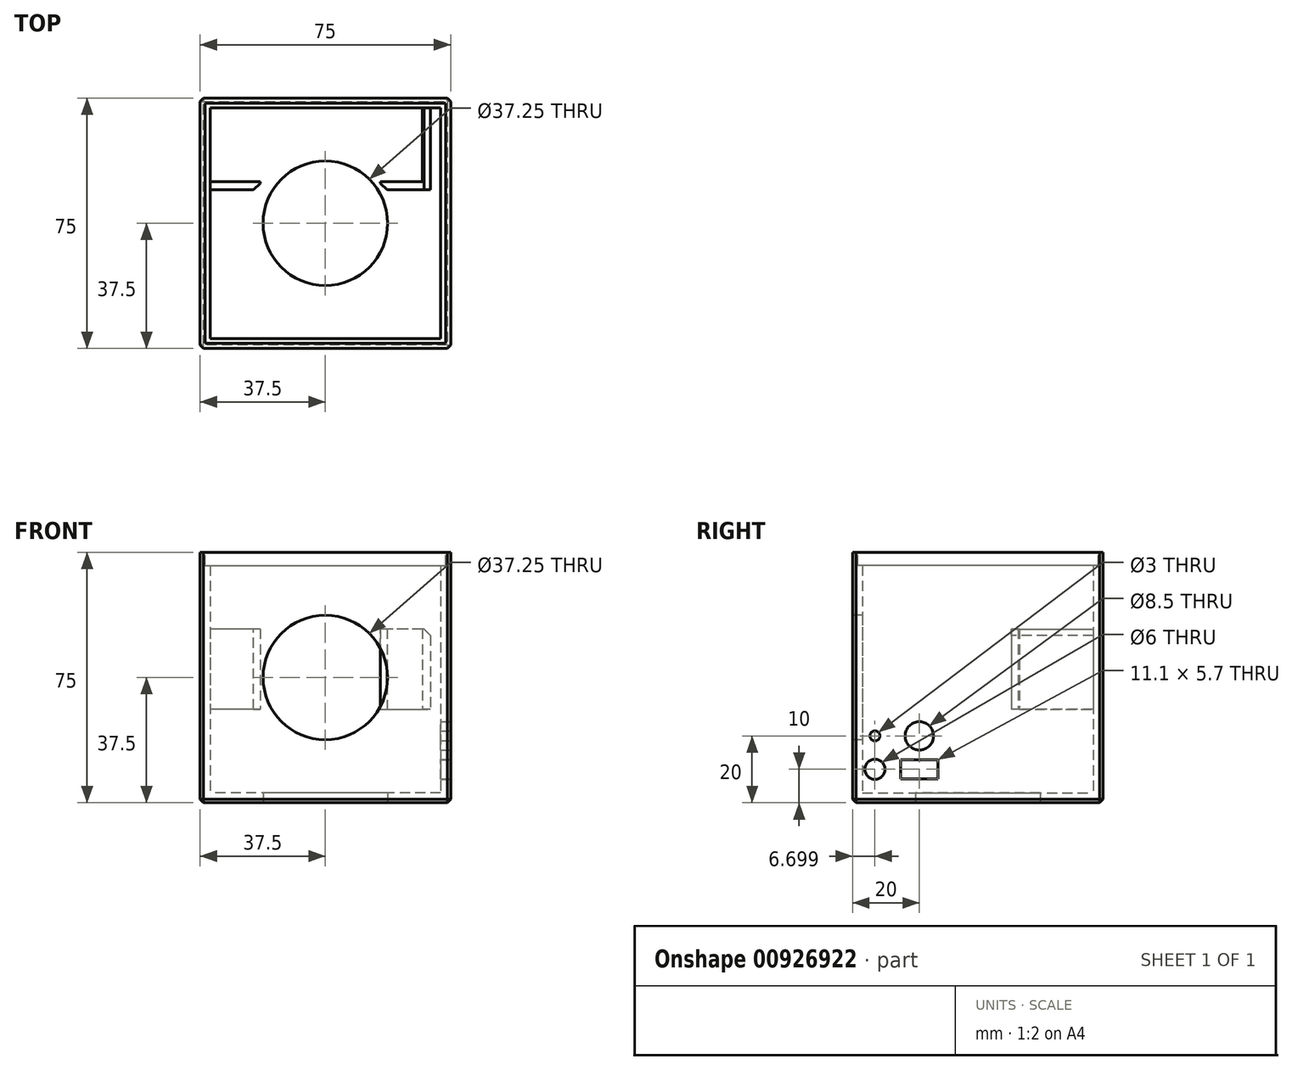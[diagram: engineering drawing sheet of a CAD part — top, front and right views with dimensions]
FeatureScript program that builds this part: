
annotation { "Feature Type Name" : "Feature", "Feature Type Description" : "" }
export const myFeature = defineFeature(function(context is Context, id is Id, definition is map)
    precondition{}
    {
        {
            var Q0;
            Q0=qCreatedBy(makeId("Top.planeOp"),FACE);
            var sketch = newSketch(context, id + "F0", { "sketchPlane" : qUnion([Q0])});
            skLineSegment(sketch, "E0.bottom", {"start": v(-37.5, 37.5) * mm, "end": v(37.5, 37.5) * mm});
            skLineSegment(sketch, "E0.top", {"start": v(-37.5, -37.5) * mm, "end": v(37.5, -37.5) * mm});
            skLineSegment(sketch, "E0.left", {"start": v(-37.5, 37.5) * mm, "end": v(-37.5, -37.5) * mm});
            skLineSegment(sketch, "E0.right", {"start": v(37.5, 37.5) * mm, "end": v(37.5, -37.5) * mm});
            skPoint(sketch, "E0.middle", {"position": v(0, 0) * mm});
            skLineSegment(sketch, "E1.0", {"start": v(-34.5, 34.5) * mm, "end": v(34.5, 34.5) * mm});
            skLineSegment(sketch, "E1.1", {"start": v(-34.5, 34.5) * mm, "end": v(-34.5, -34.5) * mm});
            skLineSegment(sketch, "E1.2", {"start": v(-34.5, -34.5) * mm, "end": v(34.5, -34.5) * mm});
            skLineSegment(sketch, "E1.3", {"start": v(34.5, 34.5) * mm, "end": v(34.5, -34.5) * mm});
            skLineSegment(sketch, "E2.right", {"start": v(29, 34.5) * mm, "end": v(29, 12.5) * mm});
            skLineSegment(sketch, "E3.0", {"start": v(31.5, 34.5) * mm, "end": v(31.5, 10) * mm});
            skLineSegment(sketch, "E4", {"start": v(-19.5, 12.5) * mm, "end": v(-19.5, 10) * mm});
            skLineSegment(sketch, "E5", {"start": v(16.5, 12.5) * mm, "end": v(16.5, 10) * mm});
            skLineSegment(sketch, "E6", {"start": v(-19.5, 10) * mm, "end": v(-34.5, 10) * mm});
            skLineSegment(sketch, "E7", {"start": v(-19.5, 12.5) * mm, "end": v(-34.5, 12.5) * mm});
            skLineSegment(sketch, "E8", {"start": v(16.5, 10) * mm, "end": v(31.5, 10) * mm});
            skLineSegment(sketch, "E9", {"start": v(16.5, 12.5) * mm, "end": v(29, 12.5) * mm});
            skCircle(sketch, "E10", {"center": v(0, 0) * mm, "radius": 18.62 * mm});
            skSolve(sketch);
        }
        {
            var Q0;
            Q0=makeQuery(id+"F0.imprint","IMPRINT",FACE,{"disambiguationData":[TD([[makeQuery(id+"F0.imprint","IMPRINT",EDGE,{"derivedFrom":sQuery(id+"F0.wireOp",EDGE,"E1.0")}),-1.0]])]});
            var Q1;
            Q1=makeQuery(id+"F0.imprint","IMPRINT",FACE,{"disambiguationData":[TD([[makeQuery(id+"F0.imprint","IMPRINT",EDGE,{"derivedFrom":sQuery(id+"F0.wireOp",EDGE,"E0.bottom")}),-1.0]])]});
            var Q2;
            {var subQ0=sQuery(id+"F0.wireOp",EDGE,"E1.2");Q2=makeQuery(id+"F0.imprint","IMPRINT",FACE,{"disambiguationData":[TD([[makeQuery(id+"F0.imprint","IMPRINT",EDGE,{"derivedFrom":subQ0}),1.0]])]});}
            var Q3;
            {var subQ0=sQuery(id+"F0.wireOp",EDGE,"E2.top");Q3=makeQuery(id+"F0.imprint","IMPRINT",FACE,{"disambiguationData":[TD([[makeQuery(id+"F0.imprint","IMPRINT",EDGE,{"derivedFrom":subQ0}),-1.0]])]});}
            extrude(context, id + "F1", {"entities" : qUnion([Q0, Q1, Q2, Q3]), "depth" : 3 * mm, "offsetDistance" : 25 * mm});
        }
        {
            var Q0;
            Q0=makeQuery(id+"F0.imprint","IMPRINT",FACE,{"disambiguationData":[TD([[makeQuery(id+"F0.imprint","IMPRINT",EDGE,{"derivedFrom":sQuery(id+"F0.wireOp",EDGE,"E0.bottom")}),-1.0]])]});
            extrude(context, id + "F2", {"entities" : qUnion([Q0]), "operationType" : NewBodyOperationType.ADD, "depth" : 75 * mm, "offsetDistance" : 25 * mm});
        }
        {
            var Q0;
            {var subQ0=sQuery(id+"F0.wireOp",EDGE,"E0.top");Q0=makeQuery(id+"F2.boolean.opBoolean","MERGE",FACE,{"derivedFrom":[makeQuery(id+"F1.opExtrude","SWEPT_FACE",FACE,{"disambiguationData":[OSD([subQ0])]}),makeQuery(id+"F2.opExtrude","SWEPT_FACE",FACE,{"disambiguationData":[OSD([subQ0])]})]});}
            var sketch = newSketch(context, id + "F3", { "sketchPlane" : qUnion([Q0])});
            skCircle(sketch, "E11", {"center": v(0, 37.5) * mm, "radius": 18.62 * mm});
            skSolve(sketch);
        }
        {
            var Q0;
            Q0=makeQuery(id+"F3.imprint","IMPRINT",FACE,{"disambiguationData":[TD([[makeQuery(id+"F3.imprint","IMPRINT",EDGE,{"derivedFrom":sQuery(id+"F3.wireOp",EDGE,"E11")}),1.0]])]});
            extrude(context, id + "F4", {"entities" : qUnion([Q0]), "operationType" : NewBodyOperationType.REMOVE, "oppositeDirection" : true, "depth" : 10.2 * mm, "offsetDistance" : 25 * mm});
        }
        {
            var Q0;
            {var subQ0=sQuery(id+"F0.wireOp",EDGE,"E2.top");Q0=makeQuery(id+"F0.imprint","IMPRINT",FACE,{"disambiguationData":[TD([[makeQuery(id+"F0.imprint","IMPRINT",EDGE,{"derivedFrom":subQ0}),-1.0]])]});}
            var Q1;
            Q1=makeQuery(id+"F0.imprint","IMPRINT",FACE,{"disambiguationData":[TD([[makeQuery(id+"F0.imprint","IMPRINT",EDGE,{"derivedFrom":sQuery(id+"F0.wireOp",EDGE,"E4")}),-1.0]])]});
            var Q2;
            {var subQ1=sQuery(id+"F0.wireOp",EDGE,"E2.right");Q2=makeQuery(id+"F0.imprint","IMPRINT",FACE,{"disambiguationData":[TD([[makeQuery(id+"F0.imprint","IMPRINT",EDGE,{"derivedFrom":subQ1}),1.0]])]});}
            extrude(context, id + "F5", {"entities" : qUnion([Q0, Q1, Q2]), "operationType" : NewBodyOperationType.ADD, "depth" : 77 * mm, "offsetDistance" : 25 * mm});
        }
        {
            var Q0;
            Q0=makeQuery(id+"F2.opExtrude","CAP_FACE",FACE,{"disambiguationData":[OSD([sQuery(id+"F0.wireOp",EDGE,"E0.bottom"),sQuery(id+"F0.wireOp",EDGE,"E0.top"),sQuery(id+"F0.wireOp",EDGE,"E0.left"),sQuery(id+"F0.wireOp",EDGE,"E0.right"),sQuery(id+"F0.wireOp",EDGE,"E1.0"),sQuery(id+"F0.wireOp",EDGE,"E1.1"),sQuery(id+"F0.wireOp",EDGE,"E1.2"),sQuery(id+"F0.wireOp",EDGE,"E1.3")])],"isStart":false});
            var sketch = newSketch(context, id + "F6", { "sketchPlane" : qUnion([Q0])});
            skLineSegment(sketch, "E12.bottom", {"start": v(-36, 36) * mm, "end": v(36, 36) * mm});
            skLineSegment(sketch, "E12.top", {"start": v(-36, -36) * mm, "end": v(36, -36) * mm});
            skLineSegment(sketch, "E12.left", {"start": v(-36, 36) * mm, "end": v(-36, -36) * mm});
            skLineSegment(sketch, "E12.right", {"start": v(36, 36) * mm, "end": v(36, -36) * mm});
            skPoint(sketch, "E12.middle", {"position": v(0, 0) * mm});
            skSolve(sketch);
        }
        {
            var Q0;
            Q0=makeQuery(id+"F6.imprint","IMPRINT",FACE,{"disambiguationData":[TD([[makeQuery(id+"F6.imprint","IMPRINT",EDGE,{"derivedFrom":sQuery(id+"F6.wireOp",EDGE,"E12.bottom")}),-1.0]])]});
            extrude(context, id + "F7", {"entities" : qUnion([Q0]), "operationType" : NewBodyOperationType.REMOVE, "oppositeDirection" : true, "depth" : 4 * mm, "offsetDistance" : 25 * mm});
        }
        {
            var Q0;
            Q0=makeQuery(id+"F1.opExtrude","CAP_EDGE",EDGE,{"disambiguationData":[OSD([sQuery(id+"F0.wireOp",EDGE,"E0.right")])],"isStart":true});
            var Q1;
            Q1=makeQuery(id+"F1.opExtrude","CAP_EDGE",EDGE,{"disambiguationData":[OSD([sQuery(id+"F0.wireOp",EDGE,"E0.top")])],"isStart":true});
            var Q2;
            {var subQ0=sQuery(id+"F0.wireOp",EDGE,"E0.left");var subQ1=sQuery(id+"F0.wireOp",EDGE,"E0.top");Q2=makeQuery(id+"F2.boolean.opBoolean","MERGE",EDGE,{"derivedFrom":[makeQuery(id+"F1.opExtrude","SWEPT_EDGE",EDGE,{"disambiguationData":[OSD([subQ1,subQ0])]}),makeQuery(id+"F2.opExtrude","SWEPT_EDGE",EDGE,{"disambiguationData":[OSD([subQ1,subQ0])]})]});}
            var Q3;
            {var subQ0=sQuery(id+"F0.wireOp",EDGE,"E0.right");var subQ1=sQuery(id+"F0.wireOp",EDGE,"E0.top");Q3=makeQuery(id+"F2.boolean.opBoolean","MERGE",EDGE,{"derivedFrom":[makeQuery(id+"F1.opExtrude","SWEPT_EDGE",EDGE,{"disambiguationData":[OSD([subQ1,subQ0])]}),makeQuery(id+"F2.opExtrude","SWEPT_EDGE",EDGE,{"disambiguationData":[OSD([subQ1,subQ0])]})]});}
            var Q4;
            Q4=makeQuery(id+"F1.opExtrude","CAP_EDGE",EDGE,{"disambiguationData":[OSD([sQuery(id+"F0.wireOp",EDGE,"E0.left")])],"isStart":true});
            var Q5;
            Q5=makeQuery(id+"F1.opExtrude","CAP_EDGE",EDGE,{"disambiguationData":[OSD([sQuery(id+"F0.wireOp",EDGE,"E0.bottom")])],"isStart":true});
            var Q6;
            {var subQ0=sQuery(id+"F0.wireOp",EDGE,"E0.right");var subQ1=sQuery(id+"F0.wireOp",EDGE,"E0.bottom");Q6=makeQuery(id+"F2.boolean.opBoolean","MERGE",EDGE,{"derivedFrom":[makeQuery(id+"F1.opExtrude","SWEPT_EDGE",EDGE,{"disambiguationData":[OSD([subQ1,subQ0])]}),makeQuery(id+"F2.opExtrude","SWEPT_EDGE",EDGE,{"disambiguationData":[OSD([subQ1,subQ0])]})]});}
            var Q7;
            {var subQ0=sQuery(id+"F0.wireOp",EDGE,"E0.left");var subQ1=sQuery(id+"F0.wireOp",EDGE,"E0.bottom");Q7=makeQuery(id+"F2.boolean.opBoolean","MERGE",EDGE,{"derivedFrom":[makeQuery(id+"F1.opExtrude","SWEPT_EDGE",EDGE,{"disambiguationData":[OSD([subQ1,subQ0])]}),makeQuery(id+"F2.opExtrude","SWEPT_EDGE",EDGE,{"disambiguationData":[OSD([subQ1,subQ0])]})]});}
            chamfer(context, id + "F8", {"entities" : qUnion([Q0, Q1, Q2, Q3, Q4, Q5, Q6, Q7]), "width" : 1 * mm});
        }
        {
            var Q0;
            Q0=makeQuery(id+"F5.opExtrude","SWEPT_FACE",FACE,{"disambiguationData":[OSD([sQuery(id+"F0.wireOp",EDGE,"E6")])]});
            var sketch = newSketch(context, id + "F9", { "sketchPlane" : qUnion([Q0])});
            skLineSegment(sketch, "E13", {"start": v(-34.5, 77) * mm, "end": v(-19.5, 77) * mm});
            skLineSegment(sketch, "E14", {"start": v(-19.5, 77) * mm, "end": v(-19.5, 52) * mm});
            skLineSegment(sketch, "E15", {"start": v(-19.5, 52) * mm, "end": v(-34.5, 52) * mm});
            skLineSegment(sketch, "E16", {"start": v(-34.5, 52) * mm, "end": v(-34.5, 77) * mm});
            skLineSegment(sketch, "E17", {"start": v(-19.5, 3) * mm, "end": v(-19.5, 28) * mm});
            skLineSegment(sketch, "E18", {"start": v(-19.5, 28) * mm, "end": v(-34.5, 28) * mm});
            skLineSegment(sketch, "E19", {"start": v(-34.5, 28) * mm, "end": v(-34.5, 3) * mm});
            skLineSegment(sketch, "E20", {"start": v(-34.5, 3) * mm, "end": v(-19.5, 3) * mm});
            skSolve(sketch);
        }
        {
            var Q0;
            Q0=makeQuery(id+"F5.opExtrude","SWEPT_FACE",FACE,{"disambiguationData":[OSD([sQuery(id+"F0.wireOp",EDGE,"E9")])]});
            var sketch = newSketch(context, id + "F10", { "sketchPlane" : qUnion([Q0])});
            skLineSegment(sketch, "E21", {"start": v(-16.5, 77) * mm, "end": v(-29, 77) * mm});
            skLineSegment(sketch, "E22", {"start": v(-29, 77) * mm, "end": v(-29, 52) * mm});
            skLineSegment(sketch, "E23", {"start": v(-29, 52) * mm, "end": v(-16.5, 52) * mm});
            skLineSegment(sketch, "E24", {"start": v(-16.5, 52) * mm, "end": v(-16.5, 77) * mm});
            skLineSegment(sketch, "E25", {"start": v(-29, 3) * mm, "end": v(-16.5, 3) * mm});
            skLineSegment(sketch, "E26", {"start": v(-16.5, 3) * mm, "end": v(-16.5, 28) * mm});
            skLineSegment(sketch, "E27", {"start": v(-16.5, 28) * mm, "end": v(-29, 28) * mm});
            skPoint(sketch, "E27.endSnap0", {"position": v(-29, 40) * mm});
            skLineSegment(sketch, "E28", {"start": v(-29, 28) * mm, "end": v(-29, 3) * mm});
            skSolve(sketch);
        }
        {
            var Q0;
            Q0=makeQuery(id+"F10.imprint","IMPRINT",FACE,{"disambiguationData":[TD([[makeQuery(id+"F10.imprint","IMPRINT",EDGE,{"derivedFrom":sQuery(id+"F10.wireOp",EDGE,"E21")}),1.0]])]});
            var Q1;
            Q1=makeQuery(id+"F10.imprint","IMPRINT",FACE,{"disambiguationData":[TD([[makeQuery(id+"F10.imprint","IMPRINT",EDGE,{"derivedFrom":sQuery(id+"F10.wireOp",EDGE,"E25")}),-1.0]])]});
            extrude(context, id + "F11", {"entities" : qUnion([Q0, Q1]), "operationType" : NewBodyOperationType.REMOVE, "oppositeDirection" : true, "depth" : 25 * mm, "offsetDistance" : 25 * mm});
        }
        {
            var Q0;
            {var subQ1=sQuery(id+"F9.wireOp",EDGE,"E13");Q0=makeQuery(id+"F9.imprint","IMPRINT",FACE,{"disambiguationData":[TD([[makeQuery(id+"F9.imprint","IMPRINT",EDGE,{"derivedFrom":subQ1}),1.0]])]});}
            var Q1;
            Q1=makeQuery(id+"F9.imprint","IMPRINT",FACE,{"disambiguationData":[TD([[makeQuery(id+"F9.imprint","IMPRINT",EDGE,{"derivedFrom":sQuery(id+"F9.wireOp",EDGE,"E17")}),-1.0]])]});
            extrude(context, id + "F12", {"entities" : qUnion([Q0, Q1]), "operationType" : NewBodyOperationType.REMOVE, "oppositeDirection" : true, "depth" : 14.8 * mm, "offsetDistance" : 25 * mm});
        }
        {
            var Q0;
            Q0=makeQuery(id+"F11.boolean.opBoolean","MERGE",FACE,{"derivedFrom":[makeQuery(id+"F5.opExtrude","SWEPT_FACE",FACE,{"disambiguationData":[OSD([sQuery(id+"F0.wireOp",EDGE,"E2.right")])]})],"fromTools":[makeQuery(id+"F11.opExtrude","SWEPT_FACE",FACE,{"disambiguationData":[OSD([sQuery(id+"F10.wireOp",EDGE,"E22")])]}),makeQuery(id+"F11.opExtrude","SWEPT_FACE",FACE,{"disambiguationData":[OSD([sQuery(id+"F10.wireOp",EDGE,"E28")])]})]});
            var sketch = newSketch(context, id + "F13", { "sketchPlane" : qUnion([Q0])});
            skLineSegment(sketch, "E29", {"start": v(-10, 52) * mm, "end": v(-34.5, 52) * mm});
            skLineSegment(sketch, "E30", {"start": v(-34.5, 52) * mm, "end": v(-34.5, 77) * mm});
            skLineSegment(sketch, "E31", {"start": v(-34.5, 77) * mm, "end": v(-10, 77) * mm});
            skLineSegment(sketch, "E32", {"start": v(-10, 77) * mm, "end": v(-10, 52) * mm});
            skLineSegment(sketch, "E33", {"start": v(-10, 28) * mm, "end": v(-34.5, 28) * mm});
            skLineSegment(sketch, "E34", {"start": v(-34.5, 28) * mm, "end": v(-34.5, 3) * mm});
            skLineSegment(sketch, "E35", {"start": v(-34.5, 3) * mm, "end": v(-10, 3) * mm});
            skLineSegment(sketch, "E36", {"start": v(-10, 3) * mm, "end": v(-10, 28) * mm});
            skSolve(sketch);
        }
        {
            var Q0;
            {var subQ6=sQuery(id+"F13.wireOp",EDGE,"E31");Q0=makeQuery(id+"F13.imprint","IMPRINT",FACE,{"disambiguationData":[TD([[makeQuery(id+"F13.imprint","IMPRINT",EDGE,{"derivedFrom":subQ6}),-1.0]])]});}
            var Q1;
            {var subQ0=sQuery(id+"F13.wireOp",EDGE,"E34");Q1=makeQuery(id+"F13.imprint","IMPRINT",FACE,{"disambiguationData":[TD([[makeQuery(id+"F13.imprint","IMPRINT",EDGE,{"derivedFrom":subQ0}),1.0]])]});}
            extrude(context, id + "F14", {"entities" : qUnion([Q0, Q1]), "operationType" : NewBodyOperationType.REMOVE, "oppositeDirection" : true, "depth" : 3.8 * mm, "offsetDistance" : 25 * mm});
        }
        {
            var Q0;
            {var subQ0=sQuery(id+"F0.wireOp",EDGE,"E0.right");Q0=makeQuery(id+"F2.boolean.opBoolean","MERGE",FACE,{"derivedFrom":[makeQuery(id+"F1.opExtrude","SWEPT_FACE",FACE,{"disambiguationData":[OSD([subQ0])]}),makeQuery(id+"F2.opExtrude","SWEPT_FACE",FACE,{"disambiguationData":[OSD([subQ0])]})]});}
            var sketch = newSketch(context, id + "F15", { "sketchPlane" : qUnion([Q0])});
            skCircle(sketch, "E37", {"center": v(-17.5, 20) * mm, "radius": 4.25 * mm});
            skLineSegment(sketch, "E38.bottom", {"start": v(-23.05, 12.85) * mm, "end": v(-11.95, 12.85) * mm});
            skLineSegment(sketch, "E38.top", {"start": v(-23.05, 7.15) * mm, "end": v(-11.95, 7.15) * mm});
            skLineSegment(sketch, "E38.left", {"start": v(-23.05, 12.85) * mm, "end": v(-23.05, 7.15) * mm});
            skLineSegment(sketch, "E38.right", {"start": v(-11.95, 12.85) * mm, "end": v(-11.95, 7.15) * mm});
            skPoint(sketch, "E38.middle", {"position": v(-17.5, 10) * mm});
            skCircle(sketch, "E39", {"center": v(-30.8, 10) * mm, "radius": 3 * mm});
            skCircle(sketch, "E40", {"center": v(-30.8, 20) * mm, "radius": 1.5 * mm});
            skSolve(sketch);
        }
        {
            var Q0;
            Q0=makeQuery(id+"F15.imprint","IMPRINT",FACE,{"disambiguationData":[TD([[makeQuery(id+"F15.imprint","IMPRINT",EDGE,{"derivedFrom":sQuery(id+"F15.wireOp",EDGE,"E40")}),1.0]])]});
            var Q1;
            Q1=makeQuery(id+"F15.imprint","IMPRINT",FACE,{"disambiguationData":[TD([[makeQuery(id+"F15.imprint","IMPRINT",EDGE,{"derivedFrom":sQuery(id+"F15.wireOp",EDGE,"E37")}),1.0]])]});
            var Q2;
            Q2=makeQuery(id+"F15.imprint","IMPRINT",FACE,{"disambiguationData":[TD([[makeQuery(id+"F15.imprint","IMPRINT",EDGE,{"derivedFrom":sQuery(id+"F15.wireOp",EDGE,"E38.bottom")}),-1.0]])]});
            var Q3;
            Q3=makeQuery(id+"F15.imprint","IMPRINT",FACE,{"disambiguationData":[TD([[makeQuery(id+"F15.imprint","IMPRINT",EDGE,{"derivedFrom":sQuery(id+"F15.wireOp",EDGE,"E39")}),1.0]])]});
            extrude(context, id + "F16", {"entities" : qUnion([Q0, Q1, Q2, Q3]), "operationType" : NewBodyOperationType.REMOVE, "oppositeDirection" : true, "depth" : 25 * mm, "offsetDistance" : 25 * mm, "hasSecondDirection" : true, "secondDirectionOppositeDirection" : false, "secondDirectionDepth" : 25 * mm});
        }
        {
            var Q0;
            Q0=makeQuery(id+"F5.opExtrude","SWEPT_EDGE",EDGE,{"disambiguationData":[OSD([sQuery(id+"F0.wireOp",EDGE,"E5"),sQuery(id+"F0.wireOp",EDGE,"E8")])]});
            var Q1;
            Q1=makeQuery(id+"F14.boolean.opBoolean","MERGE",EDGE,{"derivedFrom":[makeQuery(id+"F11.boolean.opBoolean","INTERSECT",EDGE,{"derivedFrom":[makeQuery(id+"F5.opExtrude","SWEPT_FACE",FACE,{"disambiguationData":[OSD([sQuery(id+"F0.wireOp",EDGE,"E8")])]}),makeQuery(id+"F11.opExtrude","SWEPT_FACE",FACE,{"disambiguationData":[OSD([sQuery(id+"F10.wireOp",EDGE,"E23")])]})]})],"fromTools":[makeQuery(id+"F14.opExtrude","SWEPT_EDGE",EDGE,{"disambiguationData":[OSD([sQuery(id+"F13.wireOp",EDGE,"E29"),sQuery(id+"F13.wireOp",EDGE,"E32")])]})]});
            var Q2;
            Q2=makeQuery(id+"F12.boolean.opBoolean","COPY",EDGE,{"derivedFrom":makeQuery(id+"F12.opExtrude","CAP_EDGE",EDGE,{"disambiguationData":[OSD([sQuery(id+"F9.wireOp",EDGE,"E15")])],"isStart":true})});
            var Q3;
            Q3=makeQuery(id+"F5.opExtrude","SWEPT_EDGE",EDGE,{"disambiguationData":[OSD([sQuery(id+"F0.wireOp",EDGE,"E4"),sQuery(id+"F0.wireOp",EDGE,"E6")])]});
            var Q4;
            Q4=makeQuery(id+"F14.boolean.opBoolean","INTERSECT",EDGE,{"derivedFrom":[makeQuery(id+"F5.opExtrude","SWEPT_FACE",FACE,{"disambiguationData":[OSD([sQuery(id+"F0.wireOp",EDGE,"E3.0")])]}),makeQuery(id+"F14.opExtrude","SWEPT_FACE",FACE,{"disambiguationData":[OSD([sQuery(id+"F13.wireOp",EDGE,"E29")])]})]});
            chamfer(context, id + "F17", {"entities" : qUnion([Q0, Q1, Q2, Q3, Q4]), "chamferType" : ChamferType.OFFSET_ANGLE, "width" : 2 * mm, "oppositeDirection" : false, "angle" : 45 * degree, "tangentPropagation" : true});
        }
    });
